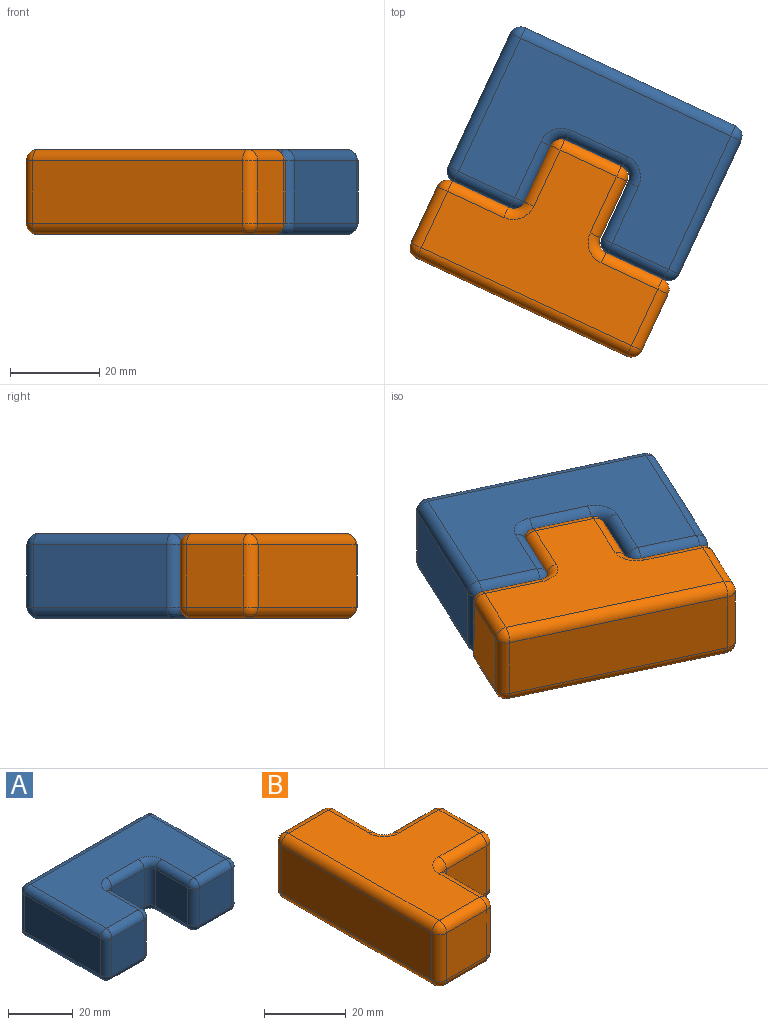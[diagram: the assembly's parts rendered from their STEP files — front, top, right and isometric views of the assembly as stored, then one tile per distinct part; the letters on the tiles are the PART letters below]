
ASSEMBLY  parts=2 mates=1
PART A: 50 faces, bbox 57.2x38.1x19.1 mm
  f0: plane 33.02x13.97mm, normal (-1,0,0), area 461.3mm2, adj f10,f13,f16,f17
  f1: plane 52.07x33.02mm, normal (0,0,-1), area 1270.8mm2, adj f10,f14,f15,f24,f25,f30,f34,f35
  f2: plane 33.02x13.97mm, normal (1,0,0), area 461.3mm2, adj f23,f24,f32,f33
  f3: plane 52.07x33.02mm, normal (0,0,1), area 1270.8mm2, adj f17,f22,f27,f32,f38,f42,f43,f46
  f4: plane 13.97x13.97mm, normal (0,-1,0), area 195.2mm2, adj f36,f37,f45,f46
  f5: plane 52.07x13.97mm, normal (0,1,0), area 727.4mm2, adj f13,f14,f22,f23
  f6: plane 13.97x13.97mm, normal (1,0,0), area 195.2mm2, adj f25,f26,f37,f38
  f7: plane 13.97x13.97mm, normal (0,-1,0), area 195.2mm2, adj f15,f16,f26,f27
  f8: plane 13.97x13.97mm, normal (-1,0,0), area 195.2mm2, adj f35,f44,f45,f49
  f9: plane 13.97x13.97mm, normal (0,-1,0), area 195.2mm2, adj f33,f34,f43,f44
  f10: cylinder r=2.54mm len=33.02mm, axis (0,-1,0), area 131.7mm2, adj f0,f1,f11,f12
  f11: sphere r=2.54mm, area 10.1mm2, adj f10,f13,f14
  f12: sphere r=2.54mm, area 10.1mm2, adj f10,f15,f16
  f13: cylinder r=2.54mm len=13.97mm, axis (0,0,-1), area 55.7mm2, adj f0,f5,f11,f18
  f14: cylinder r=2.54mm len=52.07mm, axis (1,0,0), area 207.8mm2, adj f1,f5,f11,f19
  f15: cylinder r=2.54mm len=13.97mm, axis (-1,0,0), area 55.7mm2, adj f1,f7,f12,f20
  f16: cylinder r=2.54mm len=13.97mm, axis (0,0,1), area 55.7mm2, adj f0,f7,f12,f21
  f17: cylinder r=2.54mm len=33.02mm, axis (0,1,0), area 131.7mm2, adj f0,f3,f18,f21
  f18: sphere r=2.54mm, area 10.1mm2, adj f13,f17,f22
  f19: sphere r=2.54mm, area 10.1mm2, adj f14,f23,f24
  f20: sphere r=2.54mm, area 10.1mm2, adj f15,f25,f26
  f21: sphere r=2.54mm, area 10.1mm2, adj f16,f17,f27
  f22: cylinder r=2.54mm len=52.07mm, axis (-1,0,0), area 207.8mm2, adj f3,f5,f18,f28
  f23: cylinder r=2.54mm len=13.97mm, axis (0,0,1), area 55.7mm2, adj f2,f5,f19,f28
  f24: cylinder r=2.54mm len=33.02mm, axis (0,1,0), area 131.7mm2, adj f1,f2,f19,f29
  f25: cylinder r=2.54mm len=13.97mm, axis (0,1,0), area 55.7mm2, adj f1,f6,f20,f30
  f26: cylinder r=2.54mm len=13.97mm, axis (0,0,-1), area 55.7mm2, adj f6,f7,f20,f31
  f27: cylinder r=2.54mm len=13.97mm, axis (1,0,0), area 55.7mm2, adj f3,f7,f21,f31
  f28: sphere r=2.54mm, area 10.1mm2, adj f22,f23,f32
  f29: sphere r=2.54mm, area 10.1mm2, adj f24,f33,f34
  f30: torus R=5.08mm, axis (0,0,1), area 21.7mm2, adj f1,f25,f36,f37
  f31: sphere r=2.54mm, area 10.1mm2, adj f26,f27,f38
  f32: cylinder r=2.54mm len=33.02mm, axis (0,-1,0), area 131.7mm2, adj f2,f3,f28,f39
  f33: cylinder r=2.54mm len=13.97mm, axis (0,0,-1), area 55.7mm2, adj f2,f9,f29,f39
  f34: cylinder r=2.54mm len=13.97mm, axis (-1,0,0), area 55.7mm2, adj f1,f9,f29,f40
  f35: cylinder r=2.54mm len=13.97mm, axis (0,1,0), area 55.7mm2, adj f1,f8,f40,f41
  f36: cylinder r=2.54mm len=13.97mm, axis (-1,0,0), area 55.7mm2, adj f1,f4,f30,f41
  f37: cylinder r=2.54mm len=13.97mm, axis (0,0,1), area 55.7mm2, adj f4,f6,f30,f42
  f38: cylinder r=2.54mm len=13.97mm, axis (0,-1,0), area 55.7mm2, adj f3,f6,f31,f42
  f39: sphere r=2.54mm, area 10.1mm2, adj f32,f33,f43
  f40: sphere r=2.54mm, area 10.1mm2, adj f34,f35,f44
  f41: torus R=5.08mm, axis (0,0,1), area 21.7mm2, adj f1,f35,f36,f45
  f42: torus R=5.08mm, axis (0,0,1), area 21.7mm2, adj f3,f37,f38,f46
  f43: cylinder r=2.54mm len=13.97mm, axis (1,0,0), area 55.7mm2, adj f3,f9,f39,f47
  f44: cylinder r=2.54mm len=13.97mm, axis (0,0,1), area 55.7mm2, adj f8,f9,f40,f47
  f45: cylinder r=2.54mm len=13.97mm, axis (0,0,-1), area 55.7mm2, adj f4,f8,f41,f48
  f46: cylinder r=2.54mm len=13.97mm, axis (1,0,0), area 55.7mm2, adj f3,f4,f42,f48
  f47: sphere r=2.54mm, area 10.1mm2, adj f43,f44,f49
  f48: torus R=5.08mm, axis (0,0,1), area 21.7mm2, adj f3,f45,f46,f49
  f49: cylinder r=2.54mm len=13.97mm, axis (0,-1,0), area 55.7mm2, adj f3,f8,f47,f48
PART B: 50 faces, bbox 38.1x57.2x19.1 mm
  f0: plane 52.07x33.02mm, normal (0,0,-1), area 1004.6mm2, adj f18,f19,f24,f25,f29,f35,f40,f43
  f1: plane 14.04x13.97mm, normal (1,0,0), area 196.1mm2, adj f12,f13,f19,f20
  f2: plane 52.07x13.97mm, normal (-1,0,0), area 727.4mm2, adj f14,f23,f24,f48
  f3: plane 13.97x13.9mm, normal (1,0,0), area 194.2mm2, adj f33,f34,f42,f43
  f4: plane 52.07x33.02mm, normal (0,0,1), area 1004.6mm2, adj f11,f13,f14,f16,f21,f22,f31,f32
  f5: plane 13.97x13.97mm, normal (0,-1,0), area 195.2mm2, adj f11,f12,f18,f48
  f6: plane 13.97x13.97mm, normal (0,1,0), area 195.2mm2, adj f22,f23,f34,f35
  f7: plane 13.97x13.97mm, normal (0,-1,0), area 195.2mm2, adj f20,f21,f29,f30
  f8: plane 13.97x13.97mm, normal (0,1,0), area 195.2mm2, adj f32,f41,f42,f46
  f9: plane 13.97x13.97mm, normal (1,0,0), area 195.2mm2, adj f30,f31,f40,f41
  f10: sphere r=2.54mm, area 10.1mm2, adj f11,f12,f13
  f11: cylinder r=2.54mm len=13.97mm, axis (1,0,0), area 55.7mm2, adj f4,f5,f10,f47
  f12: cylinder r=2.54mm len=13.97mm, axis (0,0,-1), area 55.7mm2, adj f1,f5,f10,f15
  f13: cylinder r=2.54mm len=14.04mm, axis (0,-1,0), area 56mm2, adj f1,f4,f10,f16
  f14: cylinder r=2.54mm len=52.07mm, axis (0,1,0), area 207.8mm2, adj f2,f4,f17,f47
  f15: sphere r=2.54mm, area 10.1mm2, adj f12,f18,f19
  f16: torus R=5.08mm, axis (0,0,1), area 21.7mm2, adj f4,f13,f20,f21
  f17: sphere r=2.54mm, area 10.1mm2, adj f14,f22,f23
  f18: cylinder r=2.54mm len=13.97mm, axis (-1,0,0), area 55.7mm2, adj f0,f5,f15,f49
  f19: cylinder r=2.54mm len=14.04mm, axis (0,1,0), area 56mm2, adj f0,f1,f15,f25
  f20: cylinder r=2.54mm len=13.97mm, axis (0,0,1), area 55.7mm2, adj f1,f7,f16,f25
  f21: cylinder r=2.54mm len=13.97mm, axis (1,0,0), area 55.7mm2, adj f4,f7,f16,f26
  f22: cylinder r=2.54mm len=13.97mm, axis (-1,0,0), area 55.7mm2, adj f4,f6,f17,f27
  f23: cylinder r=2.54mm len=13.97mm, axis (0,0,-1), area 55.7mm2, adj f2,f6,f17,f28
  f24: cylinder r=2.54mm len=52.07mm, axis (0,-1,0), area 207.8mm2, adj f0,f2,f28,f49
  f25: torus R=5.08mm, axis (0,0,1), area 21.7mm2, adj f0,f19,f20,f29
  f26: sphere r=2.54mm, area 10.1mm2, adj f21,f30,f31
  f27: sphere r=2.54mm, area 10.1mm2, adj f22,f33,f34
  f28: sphere r=2.54mm, area 10.1mm2, adj f23,f24,f35
  f29: cylinder r=2.54mm len=13.97mm, axis (-1,0,0), area 55.7mm2, adj f0,f7,f25,f36
  f30: cylinder r=2.54mm len=13.97mm, axis (0,0,1), area 55.7mm2, adj f7,f9,f26,f36
  f31: cylinder r=2.54mm len=13.97mm, axis (0,1,0), area 55.7mm2, adj f4,f9,f26,f37
  f32: cylinder r=2.54mm len=13.97mm, axis (-1,0,0), area 55.7mm2, adj f4,f8,f37,f38
  f33: cylinder r=2.54mm len=13.9mm, axis (0,-1,0), area 55.5mm2, adj f3,f4,f27,f38
  f34: cylinder r=2.54mm len=13.97mm, axis (0,0,1), area 55.7mm2, adj f3,f6,f27,f39
  f35: cylinder r=2.54mm len=13.97mm, axis (1,0,0), area 55.7mm2, adj f0,f6,f28,f39
  f36: sphere r=2.54mm, area 10.1mm2, adj f29,f30,f40
  f37: sphere r=2.54mm, area 10.1mm2, adj f31,f32,f41
  f38: torus R=5.08mm, axis (0,0,1), area 21.7mm2, adj f4,f32,f33,f42
  f39: sphere r=2.54mm, area 10.1mm2, adj f34,f35,f43
  f40: cylinder r=2.54mm len=13.97mm, axis (0,-1,0), area 55.7mm2, adj f0,f9,f36,f44
  f41: cylinder r=2.54mm len=13.97mm, axis (0,0,-1), area 55.7mm2, adj f8,f9,f37,f44
  f42: cylinder r=2.54mm len=13.97mm, axis (0,0,-1), area 55.7mm2, adj f3,f8,f38,f45
  f43: cylinder r=2.54mm len=13.9mm, axis (0,1,0), area 55.5mm2, adj f0,f3,f39,f45
  f44: sphere r=2.54mm, area 10.1mm2, adj f40,f41,f46
  f45: torus R=5.08mm, axis (0,0,1), area 21.7mm2, adj f0,f42,f43,f46
  f46: cylinder r=2.54mm len=13.97mm, axis (1,0,0), area 55.7mm2, adj f0,f8,f44,f45
  f47: sphere r=2.54mm, area 10.1mm2, adj f11,f14,f48
  f48: cylinder r=2.54mm len=13.97mm, axis (0,0,1), area 55.7mm2, adj f2,f5,f47,f49
  f49: sphere r=2.54mm, area 10.1mm2, adj f18,f24,f48
PLACE A rot(axis=(0,0,-1),25deg) t=(-13.74,28.38,-10.93)mm
PLACE B rot(axis=(0,0,1),65deg) t=(-38.17,-23.29,-10.93)mm
MATE parallel B.f9 <-> A.f4  axis (0.42,0.91,0) through (3.76,-0.8,-1.4)mm
